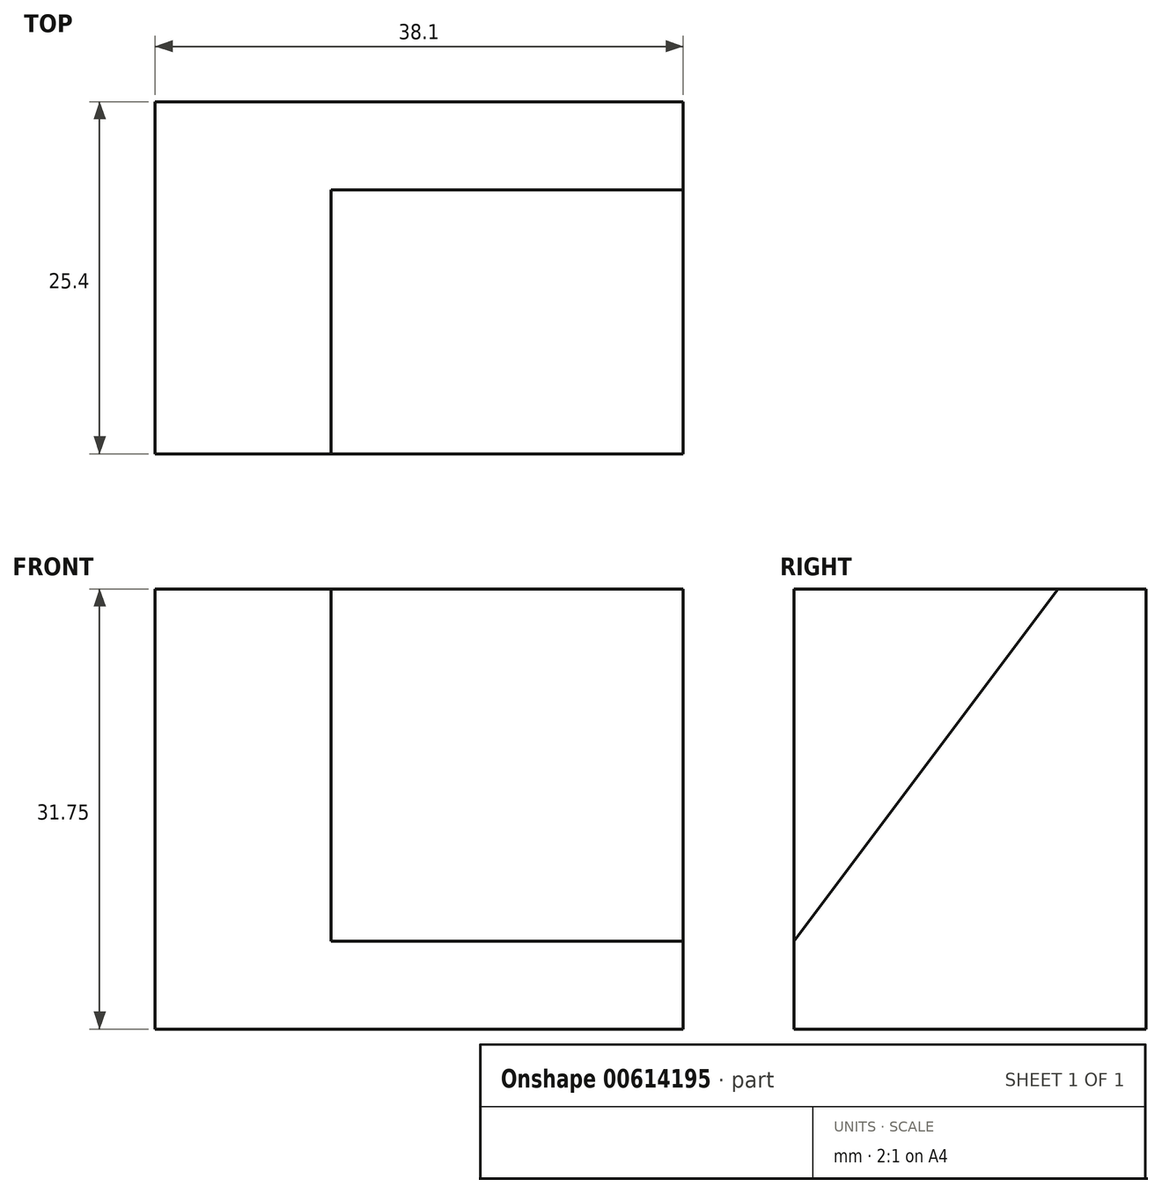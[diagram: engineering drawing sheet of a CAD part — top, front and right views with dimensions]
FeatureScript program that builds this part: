
annotation { "Feature Type Name" : "Feature", "Feature Type Description" : "" }
export const myFeature = defineFeature(function(context is Context, id is Id, definition is map)
    precondition{}
    {
        {
            var Q0;
            Q0=qCreatedBy(makeId("Front.planeOp"),FACE);
            var sketch = newSketch(context, id + "F0", { "sketchPlane" : qUnion([Q0])});
            skLineSegment(sketch, "E0", {"start": v(0, 0) * mm, "end": v(38.1, 0) * mm});
            skLineSegment(sketch, "E1", {"start": v(0, 0) * mm, "end": v(0, 31.75) * mm});
            skLineSegment(sketch, "E2", {"start": v(0, 31.75) * mm, "end": v(38.1, 31.75) * mm});
            skLineSegment(sketch, "E3", {"start": v(38.1, 31.75) * mm, "end": v(38.1, 0) * mm});
            skSolve(sketch);
        }
        {
            var Q0;
            Q0 = qSketchRegion(id + "F0", true);
            extrude(context, id + "F1", {"entities" : qUnion([Q0]), "depth" : 25.4 * mm, "offsetDistance" : 25.4 * mm});
        }
        {
            var Q0;
            Q0=makeQuery(id+"F1.opExtrude","SWEPT_FACE",FACE,{"disambiguationData":[OSD([sQuery(id+"F0.wireOp",EDGE,"E3")])]});
            var sketch = newSketch(context, id + "F2", { "sketchPlane" : qUnion([Q0])});
            skLineSegment(sketch, "E4", {"start": v(0, 31.75) * mm, "end": v(-6.35, 31.75) * mm});
            skLineSegment(sketch, "E5", {"start": v(-25.4, 0) * mm, "end": v(-25.4, 6.35) * mm});
            skLineSegment(sketch, "E6", {"start": v(-25.4, 6.35) * mm, "end": v(-6.35, 31.75) * mm});
            skSolve(sketch);
        }
        {
            var Q0;
            {var subQ0=sQuery(id+"F2.wireOp",EDGE,"E6");Q0=makeQuery(id+"F2.imprint","IMPRINT",FACE,{"disambiguationData":[TD([[makeQuery(id+"F2.imprint","IMPRINT",EDGE,{"derivedFrom":subQ0}),1.0]])]});}
            extrude(context, id + "F3", {"entities" : qUnion([Q0]), "operationType" : NewBodyOperationType.REMOVE, "oppositeDirection" : true, "depth" : 25.4 * mm, "offsetDistance" : 25.4 * mm});
        }
    });
